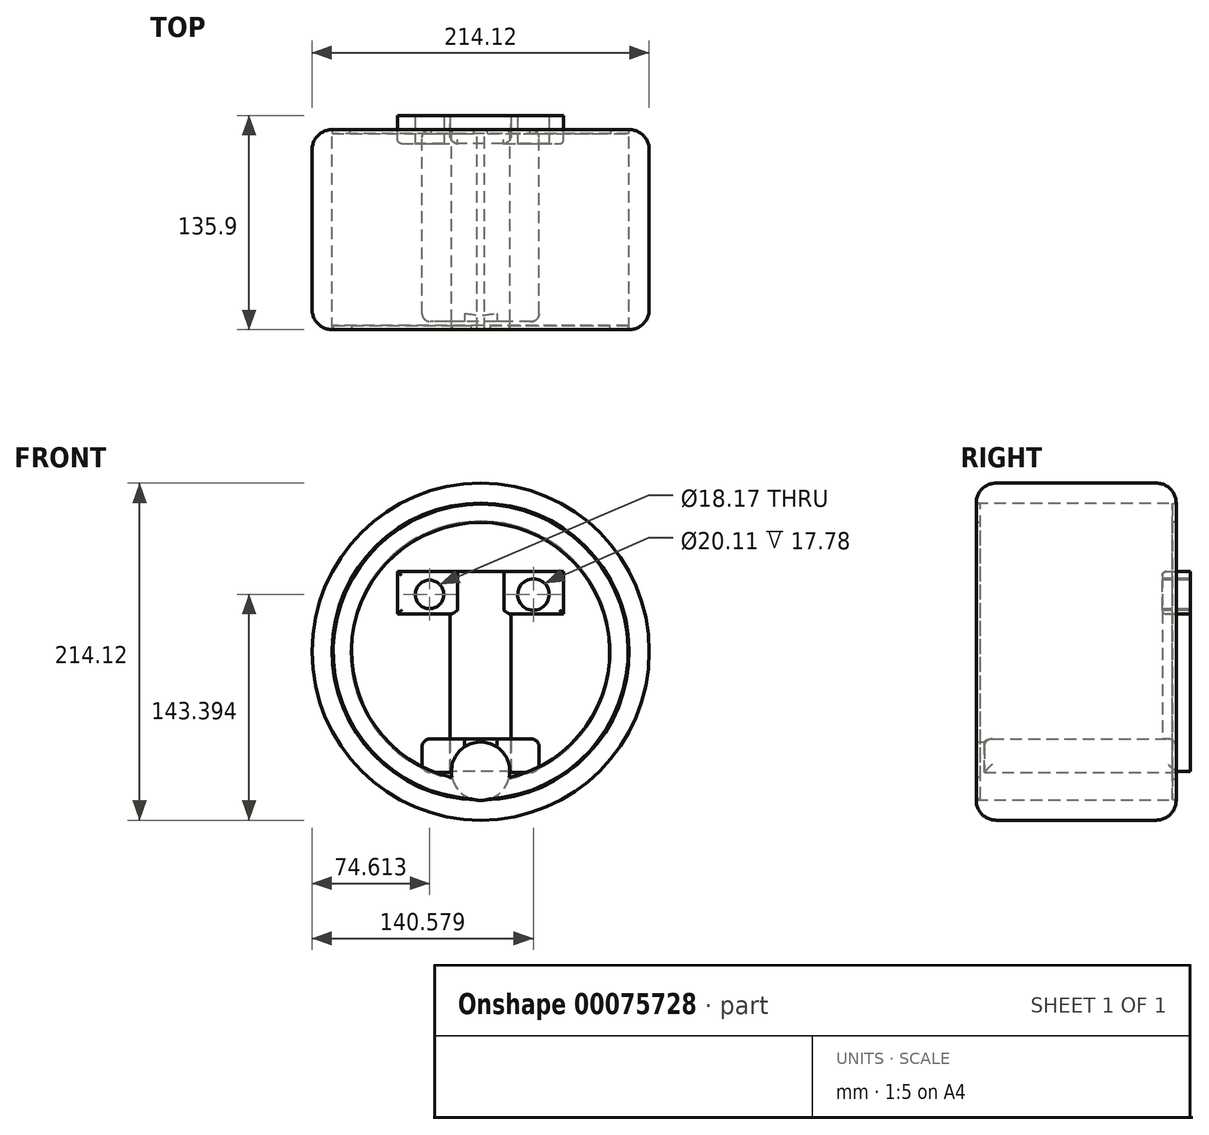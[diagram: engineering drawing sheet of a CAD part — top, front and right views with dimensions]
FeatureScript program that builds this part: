
annotation { "Feature Type Name" : "Feature", "Feature Type Description" : "" }
export const myFeature = defineFeature(function(context is Context, id is Id, definition is map)
    precondition{}
    {
        {
            var Q0;
            Q0=qCreatedBy(makeId("Front.planeOp"),FACE);
            var sketch = newSketch(context, id + "F0", { "sketchPlane" : qUnion([Q0])});
            skCircle(sketch, "E0", {"center": v(0, 0) * mm, "radius": 107.06 * mm});
            skSolve(sketch);
        }
        {
            var Q0;
            Q0=makeQuery(id+"F0.imprint","IMPRINT",FACE,{"disambiguationData":[TD([[makeQuery(id+"F0.imprint","IMPRINT",EDGE,{"derivedFrom":sQuery(id+"F0.wireOp",EDGE,"E0")}),1.0]])]});
            extrude(context, id + "F1", {"entities" : qUnion([Q0]), "depth" : 127 * mm});
        }
        {
            var Q0;
            Q0=makeQuery(id+"F1.opExtrude","CAP_EDGE",EDGE,{"disambiguationData":[OSD([sQuery(id+"F0.wireOp",EDGE,"E0")])],"isStart":false});
            var Q1;
            Q1=makeQuery(id+"F1.opExtrude","CAP_EDGE",EDGE,{"disambiguationData":[OSD([sQuery(id+"F0.wireOp",EDGE,"E0")])],"isStart":true});
            fillet(context, id + "F2", {"entities" : qUnion([Q0, Q1]), "radius" : 12.7 * mm, "tangentPropagation" : true, "allowEdgeOverflow" : false});
        }
        {
            var Q0;
            Q0=makeQuery(id+"F1.opExtrude","CAP_FACE",FACE,{"disambiguationData":[OSD([sQuery(id+"F0.wireOp",EDGE,"E0")])],"isStart":true});
            extrude(context, id + "F3", {"entities" : qUnion([Q0]), "operationType" : NewBodyOperationType.REMOVE, "oppositeDirection" : true, "depth" : 127 * mm});
        }
        {
            var Q0;
            Q0=qCreatedBy(makeId("Front.planeOp"),FACE);
            var sketch = newSketch(context, id + "F4", { "sketchPlane" : qUnion([Q0])});
            skCircle(sketch, "E1", {"center": v(0, -75.94) * mm, "radius": 18.54 * mm});
            skSolve(sketch);
        }
        {
            var Q0;
            Q0=makeQuery(id+"F4.imprint","IMPRINT",FACE,{"disambiguationData":[TD([[makeQuery(id+"F4.imprint","IMPRINT",EDGE,{"derivedFrom":sQuery(id+"F4.wireOp",EDGE,"E1")}),1.0]])]});
            extrude(context, id + "F5", {"entities" : qUnion([Q0]), "operationType" : NewBodyOperationType.ADD, "depth" : 127 * mm});
        }
        {
            var Q0;
            Q0=qCreatedBy(makeId("Front.planeOp"),FACE);
            var sketch = newSketch(context, id + "F6", { "sketchPlane" : qUnion([Q0])});
            skLineSegment(sketch, "E2.bottom", {"start": v(37.21, -55.44) * mm, "end": v(-37.21, -55.44) * mm});
            skLineSegment(sketch, "E2.top", {"start": v(37.21, -76.7) * mm, "end": v(-37.21, -76.7) * mm});
            skLineSegment(sketch, "E2.left", {"start": v(37.21, -55.44) * mm, "end": v(37.21, -76.7) * mm});
            skLineSegment(sketch, "E2.right", {"start": v(-37.21, -55.44) * mm, "end": v(-37.21, -76.7) * mm});
            skPoint(sketch, "E2.middle", {"position": v(0, -66.07) * mm});
            skSolve(sketch);
        }
        {
            var Q0;
            Q0=makeQuery(id+"F6.imprint","IMPRINT",FACE,{"disambiguationData":[TD([[makeQuery(id+"F6.imprint","IMPRINT",EDGE,{"derivedFrom":sQuery(id+"F6.wireOp",EDGE,"E2.bottom")}),1.0]])]});
            extrude(context, id + "F7", {"entities" : qUnion([Q0]), "operationType" : NewBodyOperationType.ADD, "depth" : 121.92 * mm});
        }
        {
            var Q0;
            Q0=makeQuery(id+"F7.opExtrude","SWEPT_FACE",FACE,{"disambiguationData":[OSD([sQuery(id+"F6.wireOp",EDGE,"E2.bottom")])]});
            var Q1;
            Q1=makeQuery(id+"F7.opExtrude","SWEPT_FACE",FACE,{"disambiguationData":[OSD([sQuery(id+"F6.wireOp",EDGE,"E2.right")])]});
            var Q2;
            Q2=makeQuery(id+"F7.opExtrude","SWEPT_FACE",FACE,{"disambiguationData":[OSD([sQuery(id+"F6.wireOp",EDGE,"E2.left")])]});
            fillet(context, id + "F8", {"entities" : qUnion([Q0, Q1, Q2]), "radius" : 5.08 * mm, "tangentPropagation" : true, "allowEdgeOverflow" : false});
        }
        {
            var Q0;
            Q0=qCreatedBy(makeId("Top.planeOp"),FACE);
            var sketch = newSketch(context, id + "F9", { "sketchPlane" : qUnion([Q0])});
            skLineSegment(sketch, "E3.bottom", {"start": v(19.4, 8.9) * mm, "end": v(-19.4, 8.9) * mm});
            skLineSegment(sketch, "E3.top", {"start": v(19.4, -8.9) * mm, "end": v(-19.4, -8.9) * mm});
            skLineSegment(sketch, "E3.left", {"start": v(19.4, 8.9) * mm, "end": v(19.4, -8.9) * mm});
            skLineSegment(sketch, "E3.right", {"start": v(-19.4, 8.9) * mm, "end": v(-19.4, -8.9) * mm});
            skPoint(sketch, "E3.middle", {"position": v(0, 0) * mm});
            skSolve(sketch);
        }
        {
            var Q0;
            Q0=makeQuery(id+"F9.imprint","IMPRINT",FACE,{"disambiguationData":[TD([[makeQuery(id+"F9.imprint","IMPRINT",EDGE,{"derivedFrom":sQuery(id+"F9.wireOp",EDGE,"E3.bottom")}),1.0]])]});
            extrude(context, id + "F10", {"entities" : qUnion([Q0]), "operationType" : NewBodyOperationType.ADD, "depth" : 50.8 * mm, "hasSecondDirection" : true, "secondDirectionOppositeDirection" : true, "secondDirectionDepth" : 76.2 * mm});
        }
        {
            var Q0;
            Q0=makeQuery(id+"F10.opExtrude","SWEPT_FACE",FACE,{"disambiguationData":[OSD([sQuery(id+"F9.wireOp",EDGE,"E3.bottom")])]});
            var sketch = newSketch(context, id + "F11", { "sketchPlane" : qUnion([Q0])});
            skLineSegment(sketch, "E4.bottom", {"start": v(52.7, 50.8) * mm, "end": v(-52.7, 50.8) * mm});
            skLineSegment(sketch, "E4.top", {"start": v(52.7, 23.92) * mm, "end": v(-52.7, 23.92) * mm});
            skLineSegment(sketch, "E4.left", {"start": v(52.7, 50.8) * mm, "end": v(52.7, 23.92) * mm});
            skLineSegment(sketch, "E4.right", {"start": v(-52.7, 50.8) * mm, "end": v(-52.7, 23.92) * mm});
            skPoint(sketch, "E4.middle", {"position": v(0, 37.36) * mm});
            skPoint(sketch, "E4.middle.positionSnap0", {"position": v(0, 50.8) * mm});
            skPoint(sketch, "E4.centerSnap0", {"position": v(0, 50.8) * mm});
            skSolve(sketch);
        }
        {
            var Q0;
            {var subQ3=sQuery(id+"F11.wireOp",EDGE,"E4.right");Q0=makeQuery(id+"F11.imprint","IMPRINT",FACE,{"disambiguationData":[TD([[makeQuery(id+"F11.imprint","IMPRINT",EDGE,{"derivedFrom":subQ3}),1.0]])]});}
            var Q1;
            {var subQ3=sQuery(id+"F11.wireOp",EDGE,"E4.left");Q1=makeQuery(id+"F11.imprint","IMPRINT",FACE,{"disambiguationData":[TD([[makeQuery(id+"F11.imprint","IMPRINT",EDGE,{"derivedFrom":subQ3}),-1.0]])]});}
            extrude(context, id + "F12", {"entities" : qUnion([Q0, Q1]), "operationType" : NewBodyOperationType.ADD, "oppositeDirection" : true, "depth" : 17.78 * mm});
        }
        {
            var Q0;
            Q0=qCreatedBy(makeId("Front.planeOp"),FACE);
            var sketch = newSketch(context, id + "F13", { "sketchPlane" : qUnion([Q0])});
            skCircle(sketch, "E5", {"center": v(0, 0) * mm, "radius": 94.07 * mm});
            skCircle(sketch, "E6", {"center": v(0, 0) * mm, "radius": 82.82 * mm});
            skSolve(sketch);
        }
        {
            var Q0;
            Q0=makeQuery(id+"F13.imprint","IMPRINT",FACE,{"disambiguationData":[TD([[makeQuery(id+"F13.imprint","IMPRINT",EDGE,{"derivedFrom":sQuery(id+"F13.wireOp",EDGE,"E5")}),1.0]])]});
            extrude(context, id + "F14", {"entities" : qUnion([Q0]), "operationType" : NewBodyOperationType.ADD, "depth" : 2.54 * mm});
        }
        {
            var Q0;
            Q0=makeQuery(id+"F5.opExtrude","CAP_FACE",FACE,{"disambiguationData":[OSD([sQuery(id+"F4.wireOp",EDGE,"E1")])],"isStart":false});
            var sketch = newSketch(context, id + "F15", { "sketchPlane" : qUnion([Q0])});
            skCircle(sketch, "E7", {"center": v(0, 0) * mm, "radius": 93.69 * mm});
            skCircle(sketch, "E8", {"center": v(0, 0) * mm, "radius": 82 * mm});
            skSolve(sketch);
        }
        {
            var Q0;
            {var subQ0=sQuery(id+"F15.wireOp",EDGE,"E7");var subQ1=makeQuery(id+"F5.boolean.opBoolean","SPLIT",EDGE,{"derivedFrom":makeQuery(id+"F5.opExtrude","CAP_EDGE",EDGE,{"disambiguationData":[OSD([sQuery(id+"F4.wireOp",EDGE,"E1")])],"isStart":false})});var subQ2=makeQuery(id+"F15.imprint","INTERSECT",VERTEX,{"disambiguationData":[OD(0.0)],"derivedFrom":[subQ1,subQ0]});Q0=makeQuery(id+"F15.imprint","IMPRINT",FACE,{"disambiguationData":[TD([[makeQuery(id+"F15.imprint","IMPRINT",EDGE,{"disambiguationData":[TD([[subQ2,1.0]])],"derivedFrom":subQ0}),1.0]])]});}
            extrude(context, id + "F16", {"entities" : qUnion([Q0]), "operationType" : NewBodyOperationType.ADD, "oppositeDirection" : true, "depth" : 2.54 * mm});
        }
        {
            var Q0;
            Q0=makeQuery(id+"F10.opExtrude","SWEPT_EDGE",EDGE,{"disambiguationData":[OSD([sQuery(id+"F9.wireOp",EDGE,"E3.top"),sQuery(id+"F9.wireOp",EDGE,"E3.left")])]});
            var Q1;
            Q1=makeQuery(id+"F10.opExtrude","SWEPT_EDGE",EDGE,{"disambiguationData":[OSD([sQuery(id+"F9.wireOp",EDGE,"E3.top"),sQuery(id+"F9.wireOp",EDGE,"E3.right")])]});
            fillet(context, id + "F17", {"entities" : qUnion([Q0, Q1]), "radius" : 5.08 * mm, "tangentPropagation" : true, "allowEdgeOverflow" : false});
        }
        {
            var Q0;
            Q0=makeQuery(id+"F12.opExtrude","CAP_EDGE",EDGE,{"disambiguationData":[OSD([sQuery(id+"F11.wireOp",EDGE,"E4.right")])],"isStart":false});
            var Q1;
            {var subQ0=sQuery(id+"F11.wireOp",EDGE,"E4.bottom");Q1=makeQuery(id+"F12.opExtrude","CAP_EDGE",EDGE,{"disambiguationData":[OSD([subQ0]),TDD([makeQuery(id+"F11.imprint","IMPRINT",EDGE,{"disambiguationData":[TD([[makeQuery(id+"F11.imprint","INTERSECT",VERTEX,{"derivedFrom":[makeQuery(id+"F10.opExtrude","SWEPT_EDGE",EDGE,{"disambiguationData":[OSD([sQuery(id+"F9.wireOp",EDGE,"E3.bottom"),sQuery(id+"F9.wireOp",EDGE,"E3.right")])]}),subQ0]}),1.0],[makeQuery(id+"F11.imprint","INTERSECT",VERTEX,{"derivedFrom":[subQ0,sQuery(id+"F11.wireOp",EDGE,"E4.left")]}),-1.0]])],"derivedFrom":subQ0})])],"isStart":false});}
            var Q2;
            Q2=makeQuery(id+"F12.opExtrude","CAP_EDGE",EDGE,{"disambiguationData":[OSD([sQuery(id+"F11.wireOp",EDGE,"E4.left")])],"isStart":false});
            var Q3;
            Q3=makeQuery(id+"F10.opExtrude","CAP_EDGE",EDGE,{"disambiguationData":[OSD([sQuery(id+"F9.wireOp",EDGE,"E3.top")])],"isStart":false});
            var Q4;
            {var subQ0=sQuery(id+"F11.wireOp",EDGE,"E4.top");Q4=makeQuery(id+"F12.opExtrude","CAP_EDGE",EDGE,{"disambiguationData":[OSD([subQ0]),TDD([makeQuery(id+"F11.imprint","IMPRINT",EDGE,{"disambiguationData":[TD([[makeQuery(id+"F11.imprint","INTERSECT",VERTEX,{"derivedFrom":[subQ0,sQuery(id+"F11.wireOp",EDGE,"E4.right")]}),1.0]])],"derivedFrom":subQ0})])],"isStart":false});}
            var Q5;
            {var subQ0=sQuery(id+"F11.wireOp",EDGE,"E4.top");Q5=makeQuery(id+"F12.opExtrude","CAP_EDGE",EDGE,{"disambiguationData":[OSD([subQ0]),TDD([makeQuery(id+"F11.imprint","IMPRINT",EDGE,{"disambiguationData":[TD([[makeQuery(id+"F11.imprint","INTERSECT",VERTEX,{"derivedFrom":[subQ0,sQuery(id+"F11.wireOp",EDGE,"E4.left")]}),-1.0]])],"derivedFrom":subQ0})])],"isStart":false});}
            var Q6;
            {var subQ0=sQuery(id+"F11.wireOp",EDGE,"E4.bottom");Q6=makeQuery(id+"F12.opExtrude","CAP_EDGE",EDGE,{"disambiguationData":[OSD([subQ0]),TDD([makeQuery(id+"F11.imprint","IMPRINT",EDGE,{"disambiguationData":[TD([[makeQuery(id+"F11.imprint","INTERSECT",VERTEX,{"derivedFrom":[makeQuery(id+"F10.opExtrude","SWEPT_EDGE",EDGE,{"disambiguationData":[OSD([sQuery(id+"F9.wireOp",EDGE,"E3.bottom"),sQuery(id+"F9.wireOp",EDGE,"E3.left")])]}),subQ0]}),-1.0],[makeQuery(id+"F11.imprint","INTERSECT",VERTEX,{"derivedFrom":[subQ0,sQuery(id+"F11.wireOp",EDGE,"E4.right")]}),1.0]])],"derivedFrom":subQ0})])],"isStart":false});}
            fillet(context, id + "F18", {"entities" : qUnion([Q0, Q1, Q2, Q3, Q4, Q5, Q6]), "radius" : 2.54 * mm, "tangentPropagation" : true, "allowEdgeOverflow" : false});
        }
        {
            var Q0;
            Q0=makeQuery(id+"F12.opExtrude","CAP_FACE",FACE,{"disambiguationData":[OSD([sQuery(id+"F9.wireOp",EDGE,"E3.bottom"),sQuery(id+"F9.wireOp",EDGE,"E3.right"),sQuery(id+"F11.wireOp",EDGE,"E4.bottom"),sQuery(id+"F11.wireOp",EDGE,"E4.top"),sQuery(id+"F11.wireOp",EDGE,"E4.left")])],"isStart":false});
            var sketch = newSketch(context, id + "F19", { "sketchPlane" : qUnion([Q0])});
            skCircle(sketch, "E9", {"center": v(-32.45, 36.33) * mm, "radius": 9.08 * mm});
            skPoint(sketch, "E9.centerSnap0", {"position": v(-32.45, 48.26) * mm});
            skCircle(sketch, "E10", {"center": v(33.52, 36.33) * mm, "radius": 10.05 * mm});
            skSolve(sketch);
        }
        {
            var Q0;
            Q0 = qSketchRegion(id + "F19", true);
            extrude(context, id + "F20", {"entities" : qUnion([Q0]), "operationType" : NewBodyOperationType.REMOVE, "oppositeDirection" : true, "depth" : 25.4 * mm});
        }
    });
